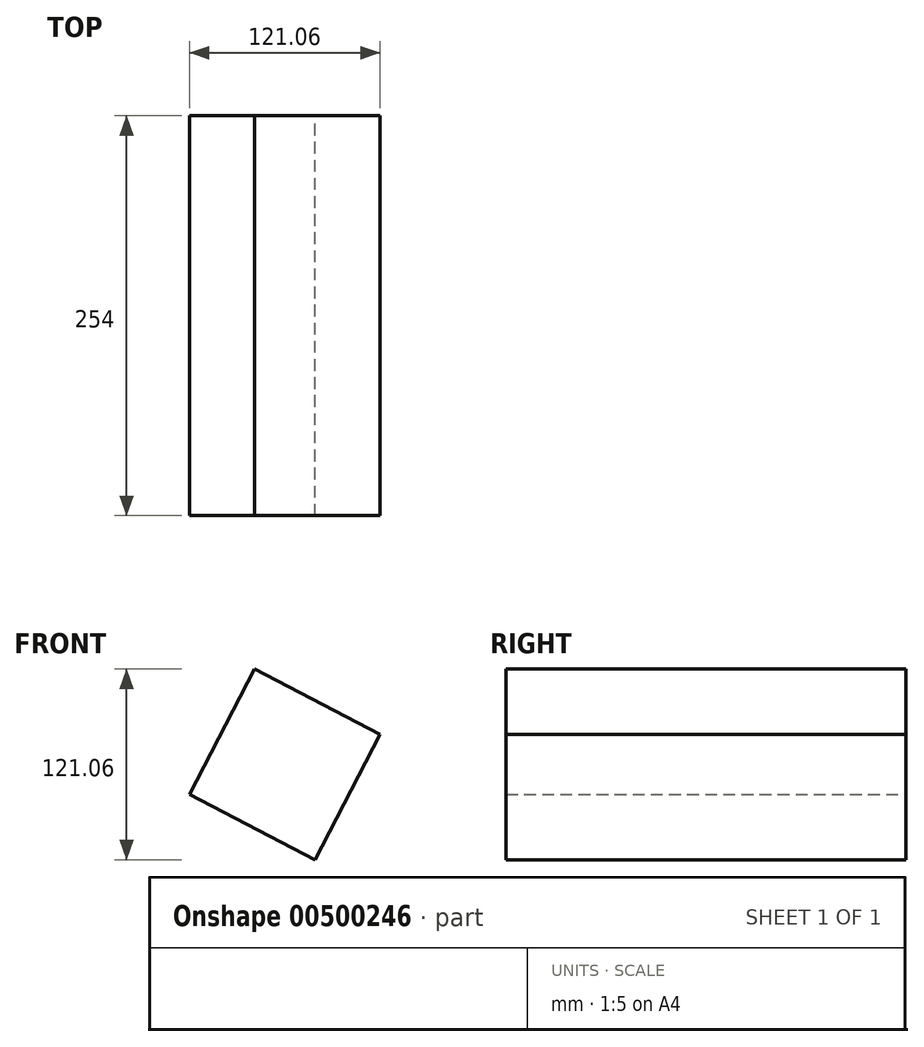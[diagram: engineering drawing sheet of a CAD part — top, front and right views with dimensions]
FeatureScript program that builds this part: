
annotation { "Feature Type Name" : "Feature", "Feature Type Description" : "" }
export const myFeature = defineFeature(function(context is Context, id is Id, definition is map)
    precondition{}
    {
        {
            var Q0;
            Q0=qCreatedBy(makeId("Front.planeOp"),FACE);
            var sketch = newSketch(context, id + "F0", { "sketchPlane" : qUnion([Q0])});
            skCircle(sketch, "E0.cCircle", {"center": v(0, 0) * mm, "radius": 63.47 * mm, "construction": true});
            skLineSegment(sketch, "E0.0", {"start": v(-60.53, -19.08) * mm, "end": v(-19.08, 60.53) * mm});
            skLineSegment(sketch, "E0.1", {"start": v(-19.08, 60.53) * mm, "end": v(60.53, 19.08) * mm});
            skLineSegment(sketch, "E0.2", {"start": v(60.53, 19.08) * mm, "end": v(19.08, -60.53) * mm});
            skLineSegment(sketch, "E0.3", {"start": v(19.08, -60.53) * mm, "end": v(-60.53, -19.08) * mm});
            skSolve(sketch);
        }
        {
            var Q0;
            Q0=makeQuery(id+"F0.imprint","IMPRINT",FACE,{"disambiguationData":[TD([[makeQuery(id+"F0.imprint","IMPRINT",EDGE,{"derivedFrom":sQuery(id+"F0.wireOp",EDGE,"E0.0")}),-1.0]])]});
            extrude(context, id + "F1", {"entities" : qUnion([Q0]), "depth" : 254 * mm, "offsetDistance" : 25 * mm});
        }
    });
